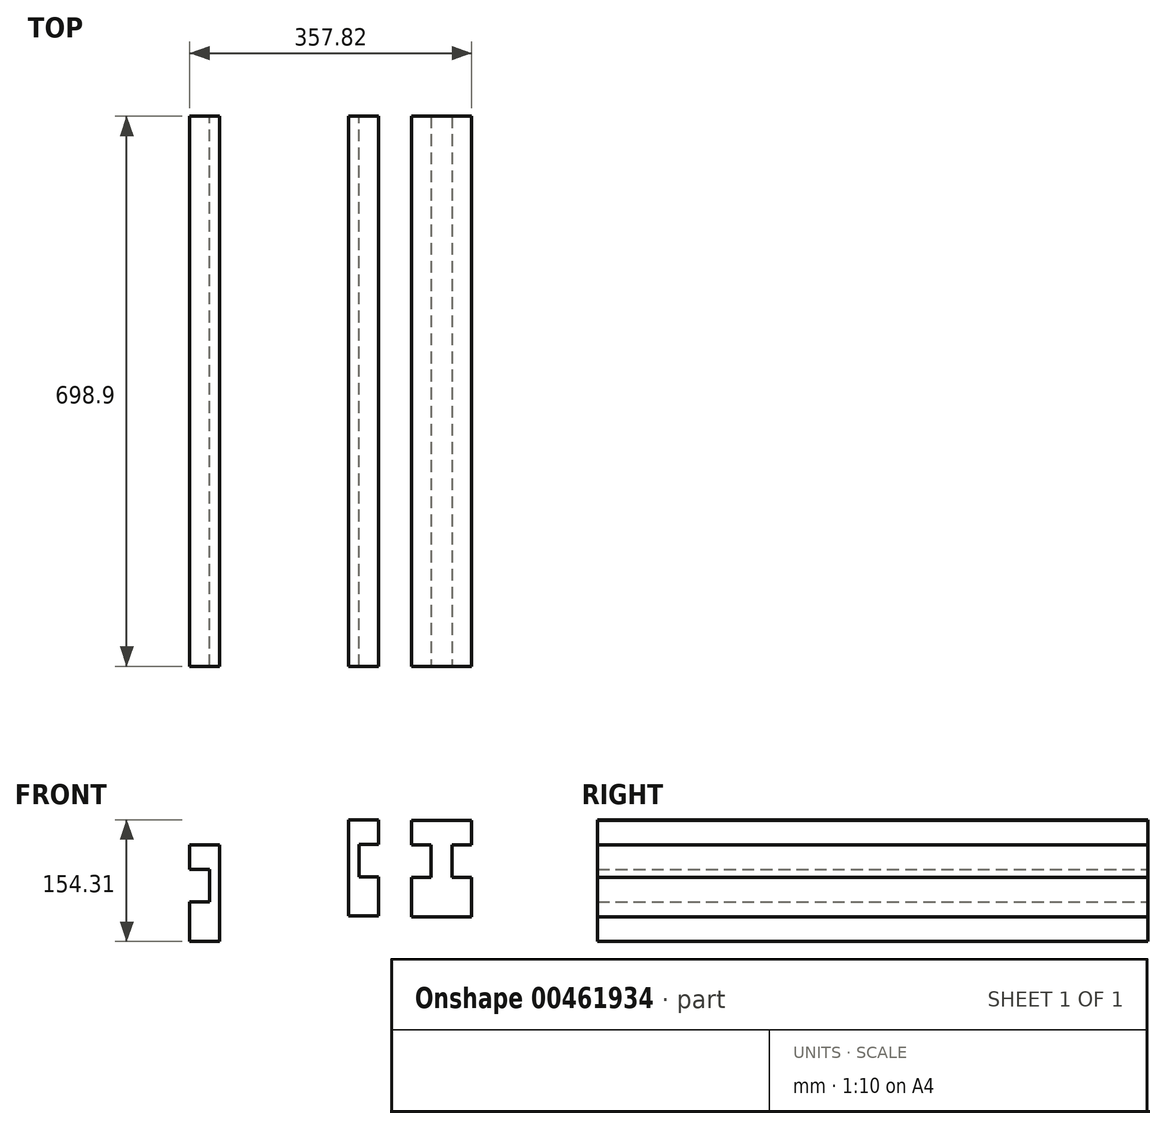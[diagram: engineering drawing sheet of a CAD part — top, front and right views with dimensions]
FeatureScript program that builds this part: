
annotation { "Feature Type Name" : "Feature", "Feature Type Description" : "" }
export const myFeature = defineFeature(function(context is Context, id is Id, definition is map)
    precondition{}
    {
        {
            var Q0;
            Q0=qCreatedBy(makeId("Front.planeOp"),FACE);
            var sketch = newSketch(context, id + "F0", { "sketchPlane" : qUnion([Q0])});
            skLineSegment(sketch, "E0.bottom", {"start": v(13.05, -61.15) * mm, "end": v(-13.05, -61.15) * mm});
            skLineSegment(sketch, "E0.top", {"start": v(13.05, 61.15) * mm, "end": v(-13.05, 61.15) * mm});
            skLineSegment(sketch, "E0.left", {"start": v(13.05, -61.15) * mm, "end": v(13.05, 61.15) * mm});
            skLineSegment(sketch, "E0.right", {"start": v(-13.05, -61.15) * mm, "end": v(-13.05, 61.15) * mm});
            skPoint(sketch, "E0.middle", {"position": v(0, 0) * mm});
            skSolve(sketch);
        }
        {
            var Q0;
            Q0=makeQuery(id+"F0.imprint","IMPRINT",FACE,{"disambiguationData":[TD([[makeQuery(id+"F0.imprint","IMPRINT",EDGE,{"derivedFrom":sQuery(id+"F0.wireOp",EDGE,"E0.bottom")}),-1.0]])]});
            extrude(context, id + "F1", {"entities" : qUnion([Q0]), "depth" : 698.9 * mm});
        }
        {
            var Q0;
            Q0=makeQuery(id+"F1.opExtrude","CAP_FACE",FACE,{"disambiguationData":[OSD([sQuery(id+"F0.wireOp",EDGE,"E0.bottom"),sQuery(id+"F0.wireOp",EDGE,"E0.top"),sQuery(id+"F0.wireOp",EDGE,"E0.left"),sQuery(id+"F0.wireOp",EDGE,"E0.right")])],"isStart":false});
            var sketch = newSketch(context, id + "F2", { "sketchPlane" : qUnion([Q0])});
            skLineSegment(sketch, "E1.bottom", {"start": v(-13.05, 61.15) * mm, "end": v(-38.05, 61.15) * mm});
            skLineSegment(sketch, "E2", {"start": v(0, 61.15) * mm, "end": v(0, -61.15) * mm, "construction": true});
            skPoint(sketch, "E3", {"position": v(-13.05, -11.15) * mm});
            skPoint(sketch, "E4", {"position": v(-13.05, 30.05) * mm});
            skLineSegment(sketch, "E5", {"start": v(-13.05, -61.15) * mm, "end": v(-38.05, -61.15) * mm});
            skLineSegment(sketch, "E6", {"start": v(-38.05, -61.15) * mm, "end": v(-38.05, -11.14) * mm});
            skLineSegment(sketch, "E7", {"start": v(-38.05, -11.14) * mm, "end": v(-13.05, -11.15) * mm});
            skLineSegment(sketch, "E8", {"start": v(-13.05, 30.05) * mm, "end": v(-38.05, 30.05) * mm});
            skLineSegment(sketch, "E9", {"start": v(-38.05, 30.05) * mm, "end": v(-38.05, 61.15) * mm});
            skLineSegment(sketch, "E10", {"start": v(-13.05, 61.15) * mm, "end": v(-13.05, 30.05) * mm});
            skLineSegment(sketch, "E11.MirrorCS", {"start": v(13.05, 61.15) * mm, "end": v(38.05, 61.15) * mm});
            skLineSegment(sketch, "E12.MirrorCS", {"start": v(38.05, 30.05) * mm, "end": v(38.05, 61.15) * mm});
            skLineSegment(sketch, "E13.MirrorCS", {"start": v(13.05, 30.05) * mm, "end": v(38.05, 30.05) * mm});
            skLineSegment(sketch, "E14.MirrorCS", {"start": v(13.05, 61.15) * mm, "end": v(13.05, 30.05) * mm});
            skLineSegment(sketch, "E15.MirrorCS", {"start": v(38.05, -11.14) * mm, "end": v(13.05, -11.15) * mm});
            skLineSegment(sketch, "E16.MirrorCS", {"start": v(38.05, -61.15) * mm, "end": v(38.05, -11.14) * mm});
            skLineSegment(sketch, "E17.MirrorCS", {"start": v(13.05, -61.15) * mm, "end": v(38.05, -61.15) * mm});
            skLineSegment(sketch, "E18", {"start": v(-13.05, -11.15) * mm, "end": v(-13.05, -61.15) * mm});
            skLineSegment(sketch, "E19", {"start": v(13.05, -11.15) * mm, "end": v(13.05, -61.15) * mm});
            skSolve(sketch);
        }
        {
            var Q0;
            Q0=qSketchRegion(id+"F2",true);
            extrude(context, id + "F3", {"entities" : qUnion([Q0]), "operationType" : NewBodyOperationType.ADD, "oppositeDirection" : true, "depth" : 698.9 * mm});
        }
        {
            var Q0;
            Q0=qCreatedBy(makeId("Front.planeOp"),FACE);
            var sketch = newSketch(context, id + "F4", { "sketchPlane" : qUnion([Q0])});
            skLineSegment(sketch, "E20", {"start": v(-117.99, 62) * mm, "end": v(-117.99, -60.3) * mm, "construction": true});
            skLineSegment(sketch, "E21.MirrorCS", {"start": v(-79.94, 30.9) * mm, "end": v(-79.94, 62) * mm});
            skLineSegment(sketch, "E22.MirrorCS", {"start": v(-104.94, 30.9) * mm, "end": v(-79.94, 30.9) * mm});
            skLineSegment(sketch, "E23.MirrorCS", {"start": v(-79.94, -10.3) * mm, "end": v(-104.94, -10.3) * mm});
            skLineSegment(sketch, "E24.MirrorCS", {"start": v(-79.94, -60.3) * mm, "end": v(-79.94, -10.3) * mm});
            skLineSegment(sketch, "E25", {"start": v(-79.94, 62) * mm, "end": v(-117.99, 62) * mm});
            skLineSegment(sketch, "E26", {"start": v(-79.94, -60.3) * mm, "end": v(-117.99, -60.3) * mm});
            skLineSegment(sketch, "E27", {"start": v(-104.94, 30.9) * mm, "end": v(-104.94, -10.3) * mm});
            skLineSegment(sketch, "E28", {"start": v(-117.99, 62) * mm, "end": v(-117.99, -60.3) * mm});
            skSolve(sketch);
        }
        {
            var Q0;
            Q0=qSketchRegion(id+"F4",true);
            extrude(context, id + "F5", {"entities" : qUnion([Q0]), "depth" : 698.9 * mm});
        }
        {
            var Q0;
            Q0=qCreatedBy(makeId("Front.planeOp"),FACE);
            var sketch = newSketch(context, id + "F6", { "sketchPlane" : qUnion([Q0])});
            skLineSegment(sketch, "E29", {"start": v(-281.72, 29.98) * mm, "end": v(-281.72, -92.32) * mm});
            skLineSegment(sketch, "E30.MirrorCS", {"start": v(-319.77, 29.98) * mm, "end": v(-281.72, 29.98) * mm});
            skLineSegment(sketch, "E31.MirrorCS", {"start": v(-319.77, -1.12) * mm, "end": v(-319.77, 29.98) * mm});
            skLineSegment(sketch, "E32.MirrorCS", {"start": v(-294.77, -1.12) * mm, "end": v(-319.77, -1.12) * mm});
            skLineSegment(sketch, "E33.MirrorCS", {"start": v(-294.77, -1.12) * mm, "end": v(-294.77, -42.32) * mm});
            skLineSegment(sketch, "E34.MirrorCS", {"start": v(-319.77, -42.3) * mm, "end": v(-294.77, -42.32) * mm});
            skLineSegment(sketch, "E35.MirrorCS", {"start": v(-319.77, -92.32) * mm, "end": v(-319.77, -42.3) * mm});
            skLineSegment(sketch, "E36.MirrorCS", {"start": v(-319.77, -92.32) * mm, "end": v(-281.72, -92.32) * mm});
            skSolve(sketch);
        }
        {
            var Q0;
            Q0=qSketchRegion(id+"F6",true);
            extrude(context, id + "F7", {"entities" : qUnion([Q0]), "depth" : 698.9 * mm});
        }
    });
